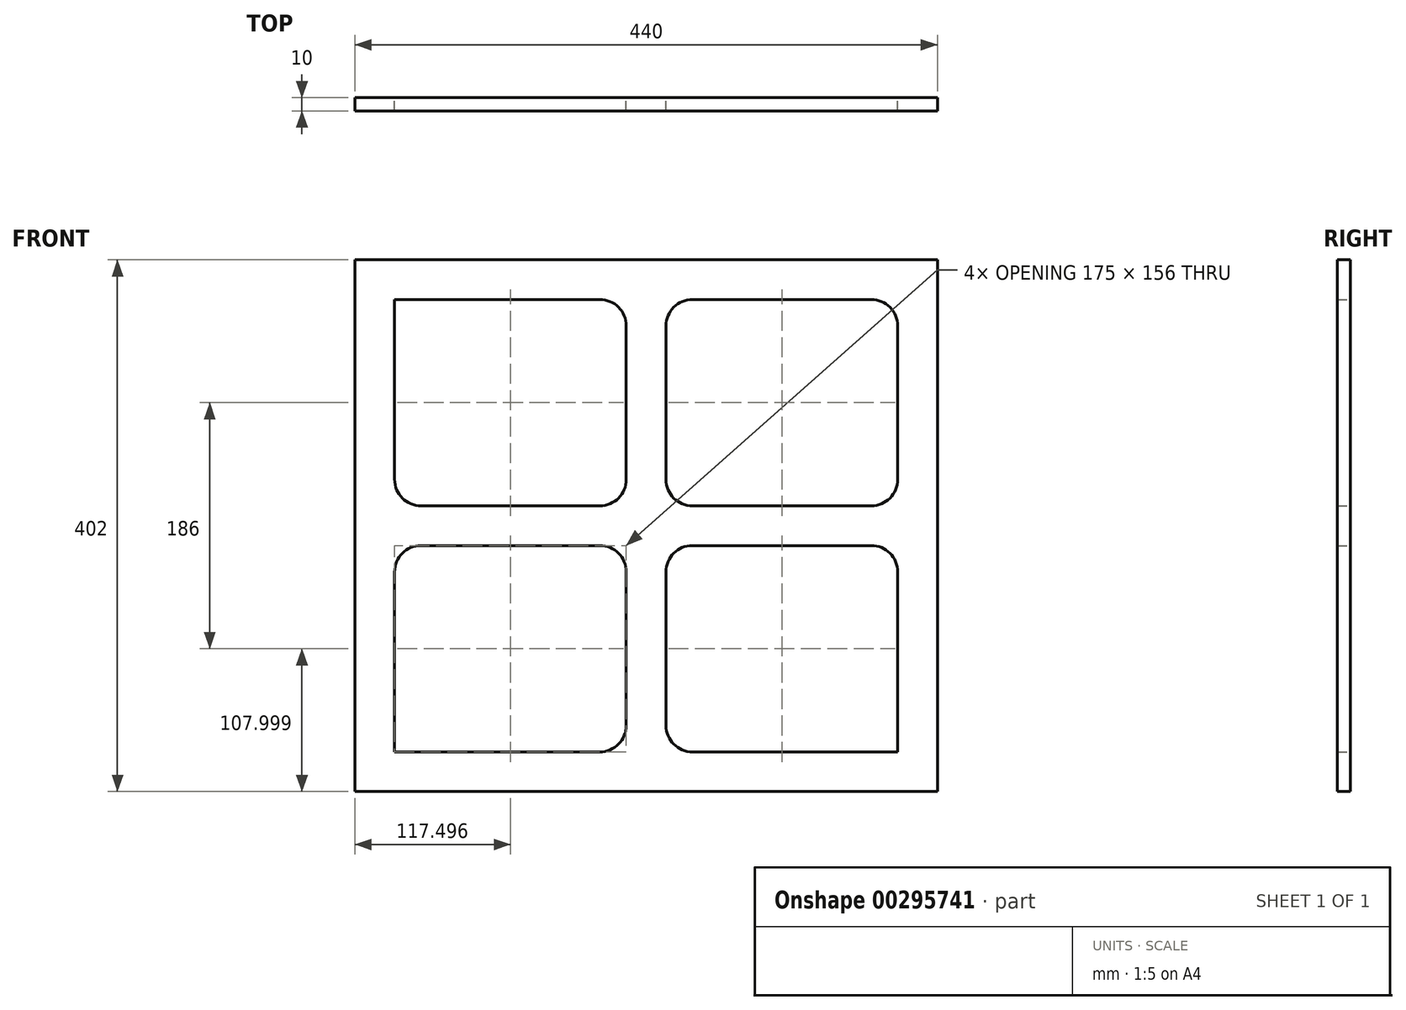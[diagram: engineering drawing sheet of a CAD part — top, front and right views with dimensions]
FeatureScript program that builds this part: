
annotation { "Feature Type Name" : "Feature", "Feature Type Description" : "" }
export const myFeature = defineFeature(function(context is Context, id is Id, definition is map)
    precondition{}
    {
        {
            var Q0;
            Q0=qCreatedBy(makeId("Front.planeOp"),FACE);
            var sketch = newSketch(context, id + "F0", { "sketchPlane" : qUnion([Q0])});
            skLineSegment(sketch, "E0.bottom", {"start": v(-256.48, 195.93) * mm, "end": v(183.52, 195.93) * mm});
            skLineSegment(sketch, "E0.top", {"start": v(-256.48, -206.07) * mm, "end": v(183.52, -206.07) * mm});
            skLineSegment(sketch, "E0.left", {"start": v(-256.48, 195.93) * mm, "end": v(-256.48, -206.07) * mm});
            skLineSegment(sketch, "E0.right", {"start": v(183.52, 195.93) * mm, "end": v(183.52, -206.07) * mm});
            skLineSegment(sketch, "E1.bottom", {"start": v(153.52, 165.93) * mm, "end": v(-21.48, 165.93) * mm});
            skLineSegment(sketch, "E1.top", {"start": v(153.52, -176.07) * mm, "end": v(-21.48, -176.07) * mm});
            skLineSegment(sketch, "E1.left", {"start": v(153.52, 165.93) * mm, "end": v(153.52, 9.93) * mm});
            skLineSegment(sketch, "E1.right", {"start": v(-226.48, 165.93) * mm, "end": v(-226.48, 9.93) * mm});
            skLineSegment(sketch, "E2", {"start": v(-36.48, 165.93) * mm, "end": v(-36.48, -176.07) * mm, "construction": true});
            skLineSegment(sketch, "E3.top", {"start": v(153.52, 9.93) * mm, "end": v(-21.48, 9.93) * mm});
            skLineSegment(sketch, "E3.right", {"start": v(-21.48, 165.93) * mm, "end": v(-21.48, 9.93) * mm});
            skLineSegment(sketch, "E4.top", {"start": v(153.52, -20.07) * mm, "end": v(-21.48, -20.07) * mm});
            skLineSegment(sketch, "E4.left", {"start": v(153.52, -176.07) * mm, "end": v(153.52, -20.07) * mm});
            skLineSegment(sketch, "E4.right", {"start": v(-21.48, -176.07) * mm, "end": v(-21.48, -20.07) * mm});
            skLineSegment(sketch, "E5.bottom", {"start": v(-226.48, -176.07) * mm, "end": v(-51.48, -176.07) * mm});
            skLineSegment(sketch, "E5.top", {"start": v(-226.48, -20.07) * mm, "end": v(-51.48, -20.07) * mm});
            skLineSegment(sketch, "E5.left", {"start": v(-226.48, -176.07) * mm, "end": v(-226.48, -20.07) * mm});
            skLineSegment(sketch, "E5.right", {"start": v(-51.48, -176.07) * mm, "end": v(-51.48, -20.07) * mm});
            skLineSegment(sketch, "E6.bottom", {"start": v(-226.48, 165.93) * mm, "end": v(-51.48, 165.93) * mm});
            skLineSegment(sketch, "E6.top", {"start": v(-226.48, 9.93) * mm, "end": v(-51.48, 9.93) * mm});
            skLineSegment(sketch, "E6.right", {"start": v(-51.48, 165.93) * mm, "end": v(-51.48, 9.93) * mm});
            skLineSegment(sketch, "E7.trimOffspring", {"start": v(-51.48, 165.93) * mm, "end": v(-226.48, 165.93) * mm});
            skLineSegment(sketch, "E8.trimOffspring", {"start": v(153.52, -20.07) * mm, "end": v(153.52, -176.07) * mm});
            skLineSegment(sketch, "E9.trimOffspring", {"start": v(-51.48, -176.07) * mm, "end": v(-226.48, -176.07) * mm});
            skLineSegment(sketch, "E10.trimOffspring", {"start": v(-226.48, -20.07) * mm, "end": v(-226.48, -176.07) * mm});
            skLineSegment(sketch, "E11", {"start": v(192.47, -5.07) * mm, "end": v(-275.82, -5.07) * mm, "construction": true});
            skPoint(sketch, "E11.startSnap0", {"position": v(183.52, -5.07) * mm});
            skSolve(sketch);
        }
        {
            var Q0;
            Q0 = qSketchRegion(id + "F0", true);
            extrude(context, id + "F1", {"entities" : qUnion([Q0]), "depth" : 10 * mm});
        }
        {
            var Q0;
            Q0=makeQuery(id+"F1.opExtrude","SWEPT_EDGE",EDGE,{"disambiguationData":[OSD([sQuery(id+"F0.wireOp",EDGE,"E1.bottom"),sQuery(id+"F0.wireOp",EDGE,"E1.left")])]});
            var Q1;
            Q1=makeQuery(id+"F1.opExtrude","SWEPT_EDGE",EDGE,{"disambiguationData":[OSD([sQuery(id+"F0.wireOp",EDGE,"E1.bottom"),sQuery(id+"F0.wireOp",EDGE,"E3.right")])]});
            var Q2;
            Q2=makeQuery(id+"F1.opExtrude","SWEPT_EDGE",EDGE,{"disambiguationData":[OSD([sQuery(id+"F0.wireOp",EDGE,"E1.right"),sQuery(id+"F0.wireOp",EDGE,"E7.trimOffspring")])]});
            var Q3;
            Q3=makeQuery(id+"F1.opExtrude","SWEPT_EDGE",EDGE,{"disambiguationData":[OSD([sQuery(id+"F0.wireOp",EDGE,"E5.top"),sQuery(id+"F0.wireOp",EDGE,"E10.trimOffspring")])]});
            var Q4;
            Q4=makeQuery(id+"F1.opExtrude","SWEPT_EDGE",EDGE,{"disambiguationData":[OSD([sQuery(id+"F0.wireOp",EDGE,"E4.top"),sQuery(id+"F0.wireOp",EDGE,"E4.right")])]});
            var Q5;
            Q5=makeQuery(id+"F1.opExtrude","SWEPT_EDGE",EDGE,{"disambiguationData":[OSD([sQuery(id+"F0.wireOp",EDGE,"E6.right"),sQuery(id+"F0.wireOp",EDGE,"E7.trimOffspring")])]});
            var Q6;
            Q6=makeQuery(id+"F1.opExtrude","SWEPT_EDGE",EDGE,{"disambiguationData":[OSD([sQuery(id+"F0.wireOp",EDGE,"E6.top"),sQuery(id+"F0.wireOp",EDGE,"E6.right")])]});
            var Q7;
            Q7=makeQuery(id+"F1.opExtrude","SWEPT_EDGE",EDGE,{"disambiguationData":[OSD([sQuery(id+"F0.wireOp",EDGE,"E5.right"),sQuery(id+"F0.wireOp",EDGE,"E9.trimOffspring")])]});
            var Q8;
            Q8=makeQuery(id+"F1.opExtrude","SWEPT_EDGE",EDGE,{"disambiguationData":[OSD([sQuery(id+"F0.wireOp",EDGE,"E1.top"),sQuery(id+"F0.wireOp",EDGE,"E8.trimOffspring")])]});
            var Q9;
            Q9=makeQuery(id+"F1.opExtrude","SWEPT_EDGE",EDGE,{"disambiguationData":[OSD([sQuery(id+"F0.wireOp",EDGE,"E3.top"),sQuery(id+"F0.wireOp",EDGE,"E1.left")])]});
            var Q10;
            Q10=makeQuery(id+"F1.opExtrude","SWEPT_EDGE",EDGE,{"disambiguationData":[OSD([sQuery(id+"F0.wireOp",EDGE,"E9.trimOffspring"),sQuery(id+"F0.wireOp",EDGE,"E10.trimOffspring")])]});
            var Q11;
            Q11=makeQuery(id+"F1.opExtrude","SWEPT_EDGE",EDGE,{"disambiguationData":[OSD([sQuery(id+"F0.wireOp",EDGE,"E6.top"),sQuery(id+"F0.wireOp",EDGE,"E1.right")])]});
            var Q12;
            Q12=makeQuery(id+"F1.opExtrude","SWEPT_EDGE",EDGE,{"disambiguationData":[OSD([sQuery(id+"F0.wireOp",EDGE,"E1.top"),sQuery(id+"F0.wireOp",EDGE,"E4.right")])]});
            var Q13;
            Q13=makeQuery(id+"F1.opExtrude","SWEPT_EDGE",EDGE,{"disambiguationData":[OSD([sQuery(id+"F0.wireOp",EDGE,"E3.top"),sQuery(id+"F0.wireOp",EDGE,"E3.right")])]});
            var Q14;
            Q14=makeQuery(id+"F1.opExtrude","SWEPT_EDGE",EDGE,{"disambiguationData":[OSD([sQuery(id+"F0.wireOp",EDGE,"E5.top"),sQuery(id+"F0.wireOp",EDGE,"E5.right")])]});
            var Q15;
            Q15=makeQuery(id+"F1.opExtrude","SWEPT_EDGE",EDGE,{"disambiguationData":[OSD([sQuery(id+"F0.wireOp",EDGE,"E4.top"),sQuery(id+"F0.wireOp",EDGE,"E8.trimOffspring")])]});
            fillet(context, id + "F2", {"entities" : qUnion([Q0, Q1, Q2, Q3, Q4, Q5, Q6, Q7, Q8, Q9, Q10, Q11, Q12, Q13, Q14, Q15]), "radius" : 20 * mm, "tangentPropagation" : true, "allowEdgeOverflow" : false});
        }
    });
